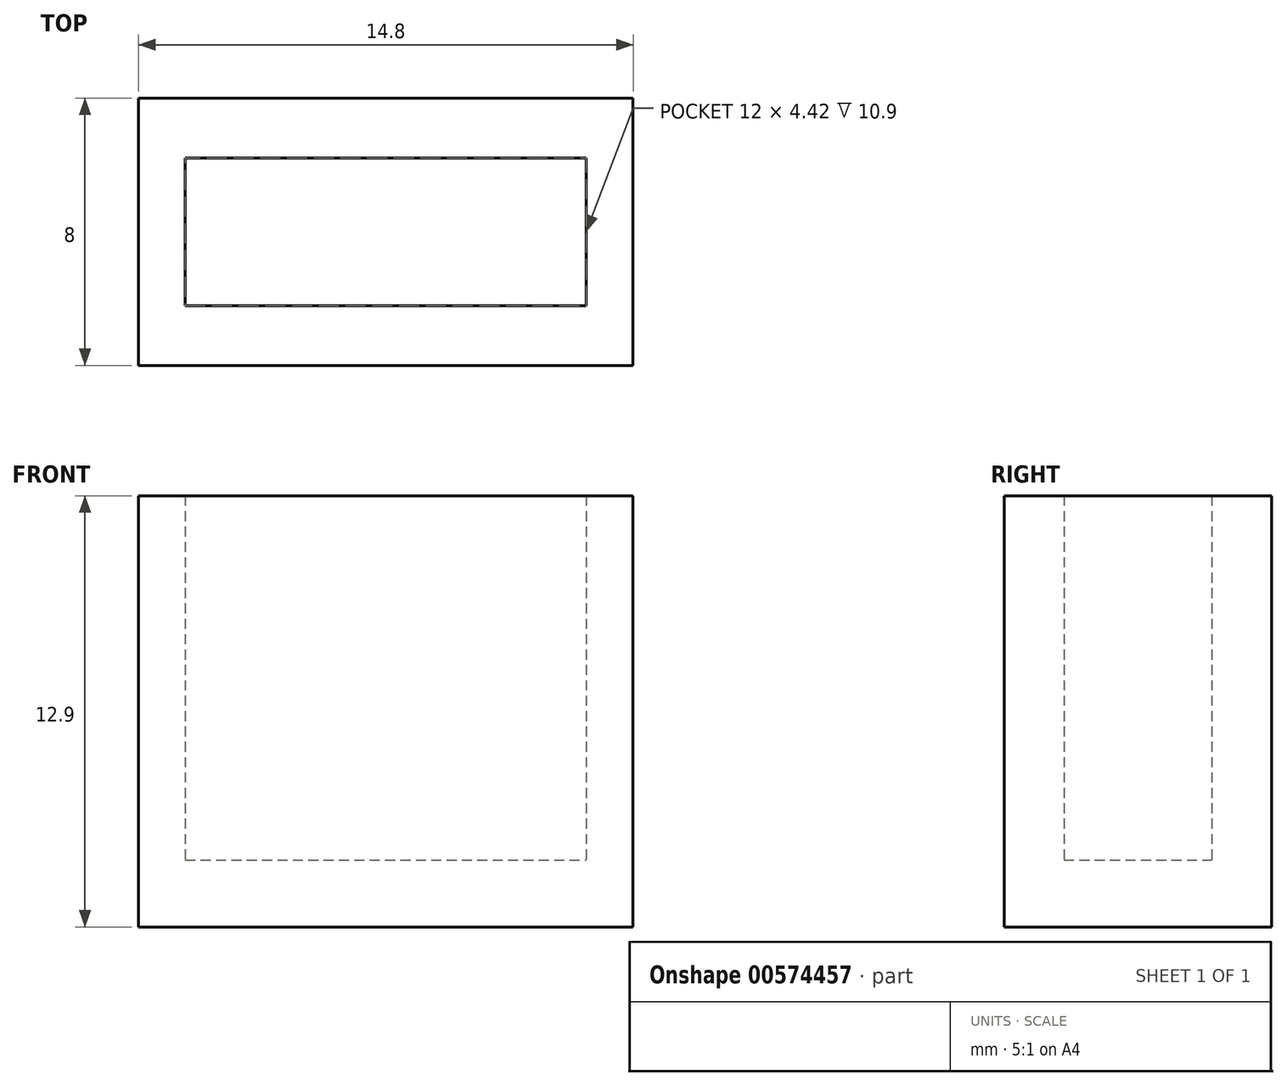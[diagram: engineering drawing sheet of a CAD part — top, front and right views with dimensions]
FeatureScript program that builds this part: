
annotation { "Feature Type Name" : "Feature", "Feature Type Description" : "" }
export const myFeature = defineFeature(function(context is Context, id is Id, definition is map)
    precondition{}
    {
        {
            var Q0;
            Q0=qCreatedBy(makeId("Top.planeOp"),FACE);
            var sketch = newSketch(context, id + "F0", { "sketchPlane" : qUnion([Q0])});
            skLineSegment(sketch, "E0.bottom", {"start": v(-15.84, 8.23) * mm, "end": v(-1.04, 8.23) * mm});
            skLineSegment(sketch, "E0.top", {"start": v(-15.84, 0.23) * mm, "end": v(-1.04, 0.23) * mm});
            skLineSegment(sketch, "E0.left", {"start": v(-15.84, 8.23) * mm, "end": v(-15.84, 0.23) * mm});
            skLineSegment(sketch, "E0.right", {"start": v(-1.04, 8.23) * mm, "end": v(-1.04, 0.23) * mm});
            skPoint(sketch, "E1", {"position": v(-14.44, 0.23) * mm});
            skPoint(sketch, "E2", {"position": v(-2.44, 0.23) * mm});
            skPoint(sketch, "E3", {"position": v(-15.84, 2.02) * mm});
            skPoint(sketch, "E4", {"position": v(-15.84, 6.44) * mm});
            skLineSegment(sketch, "E5", {"start": v(-14.44, 2.02) * mm, "end": v(-14.44, 6.44) * mm});
            skLineSegment(sketch, "E6", {"start": v(-2.44, 2.02) * mm, "end": v(-2.44, 6.44) * mm});
            skLineSegment(sketch, "E7", {"start": v(-14.44, 6.44) * mm, "end": v(-2.44, 6.44) * mm});
            skLineSegment(sketch, "E8", {"start": v(-14.44, 2.02) * mm, "end": v(-2.44, 2.02) * mm});
            skPoint(sketch, "E9.orphan", {"position": v(-2.44, 8.23) * mm});
            skPoint(sketch, "E10.orphan", {"position": v(-14.44, 8.23) * mm});
            skSolve(sketch);
        }
        {
            var Q0;
            Q0=makeQuery(id+"F0.imprint","IMPRINT",FACE,{"disambiguationData":[TD([[makeQuery(id+"F0.imprint","IMPRINT",EDGE,{"derivedFrom":sQuery(id+"F0.wireOp",EDGE,"E5")}),-1.0]])]});
            extrude(context, id + "F1", {"entities" : qUnion([Q0]), "depth" : 2 * mm, "offsetDistance" : 25 * mm});
        }
        {
            var Q0;
            Q0 = qSketchRegion(id + "F0", true);
            extrude(context, id + "F2", {"entities" : qUnion([Q0]), "operationType" : NewBodyOperationType.ADD, "depth" : 12.9 * mm, "offsetDistance" : 25 * mm});
        }
    });
